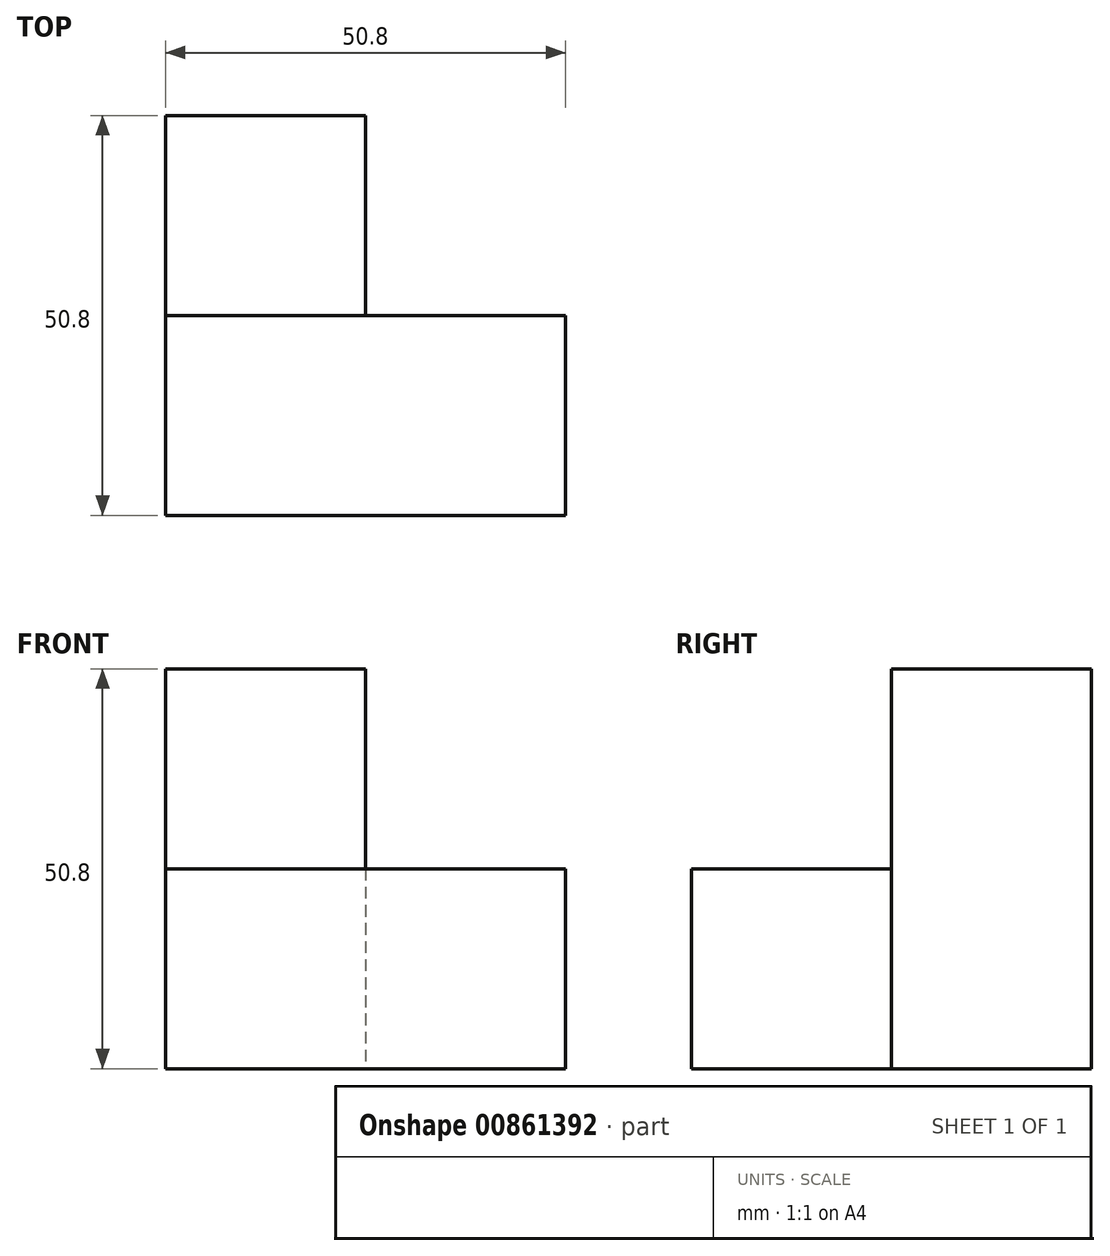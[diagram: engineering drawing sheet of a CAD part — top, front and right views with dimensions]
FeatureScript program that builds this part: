
annotation { "Feature Type Name" : "Feature", "Feature Type Description" : "" }
export const myFeature = defineFeature(function(context is Context, id is Id, definition is map)
    precondition{}
    {
        {
            var Q0;
            Q0=qCreatedBy(makeId("Top.planeOp"),FACE);
            var sketch = newSketch(context, id + "F0", { "sketchPlane" : qUnion([Q0])});
            skLineSegment(sketch, "E0.bottom", {"start": v(12.7, -25.4) * mm, "end": v(-12.7, -25.4) * mm});
            skLineSegment(sketch, "E0.top", {"start": v(12.7, 25.4) * mm, "end": v(-12.7, 25.4) * mm});
            skLineSegment(sketch, "E0.left", {"start": v(12.7, 0) * mm, "end": v(12.7, 25.4) * mm});
            skLineSegment(sketch, "E0.right", {"start": v(-12.7, -25.4) * mm, "end": v(-12.7, 25.4) * mm});
            skPoint(sketch, "E0.middle", {"position": v(0, 0) * mm});
            skLineSegment(sketch, "E1.bottom", {"start": v(12.7, 0) * mm, "end": v(38.1, 0) * mm});
            skLineSegment(sketch, "E1.top", {"start": v(12.7, -25.4) * mm, "end": v(38.1, -25.4) * mm});
            skLineSegment(sketch, "E1.right", {"start": v(38.1, 0) * mm, "end": v(38.1, -25.4) * mm});
            skSolve(sketch);
        }
        {
            var Q0;
            Q0 = qSketchRegion(id + "F0", true);
            extrude(context, id + "F1", {"entities" : qUnion([Q0]), "depth" : 25.4 * mm, "offsetDistance" : 25.4 * mm});
        }
        {
            var Q0;
            Q0=makeQuery(id+"F1.opExtrude","CAP_FACE",FACE,{"disambiguationData":[OSD([sQuery(id+"F0.wireOp",EDGE,"E0.bottom"),sQuery(id+"F0.wireOp",EDGE,"E0.top"),sQuery(id+"F0.wireOp",EDGE,"E0.left"),sQuery(id+"F0.wireOp",EDGE,"E0.right"),sQuery(id+"F0.wireOp",EDGE,"E1.bottom"),sQuery(id+"F0.wireOp",EDGE,"E1.top"),sQuery(id+"F0.wireOp",EDGE,"E1.right")])],"isStart":false});
            var sketch = newSketch(context, id + "F2", { "sketchPlane" : qUnion([Q0])});
            skLineSegment(sketch, "E2.bottom", {"start": v(-12.7, 25.4) * mm, "end": v(12.7, 25.4) * mm});
            skLineSegment(sketch, "E2.top", {"start": v(-12.7, 0) * mm, "end": v(12.7, 0) * mm});
            skLineSegment(sketch, "E2.left", {"start": v(-12.7, 25.4) * mm, "end": v(-12.7, 0) * mm});
            skLineSegment(sketch, "E2.right", {"start": v(12.7, 25.4) * mm, "end": v(12.7, 0) * mm});
            skSolve(sketch);
        }
        {
            var Q0;
            Q0 = qSketchRegion(id + "F2", true);
            extrude(context, id + "F3", {"entities" : qUnion([Q0]), "operationType" : NewBodyOperationType.ADD, "depth" : 25.4 * mm, "offsetDistance" : 25.4 * mm});
        }
    });
